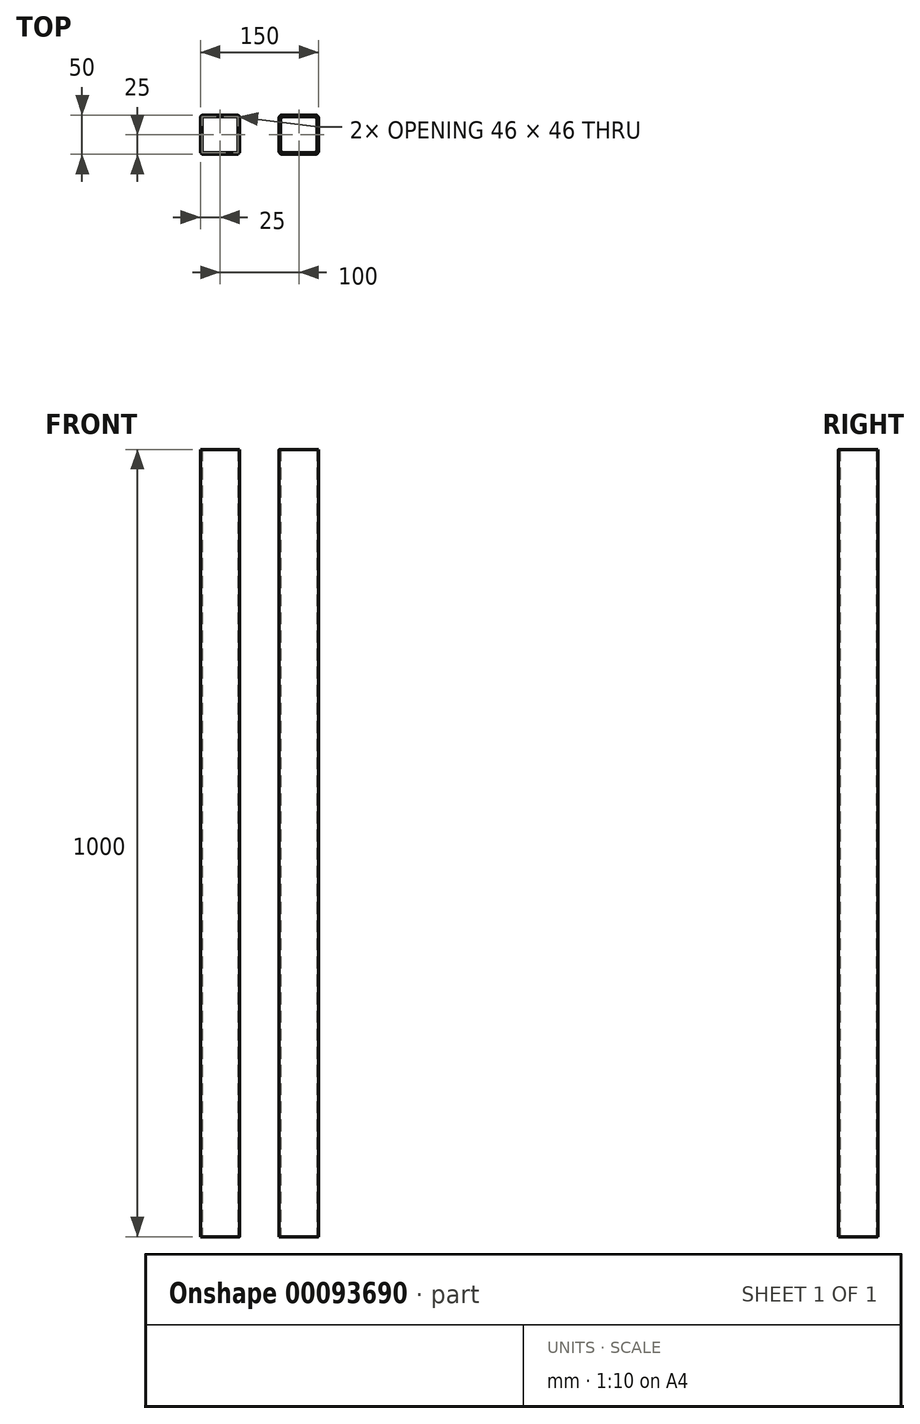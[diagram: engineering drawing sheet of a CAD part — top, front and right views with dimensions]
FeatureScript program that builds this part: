
annotation { "Feature Type Name" : "Feature", "Feature Type Description" : "" }
export const myFeature = defineFeature(function(context is Context, id is Id, definition is map)
    precondition{}
    {
        {
            var Q0;
            Q0=qCreatedBy(makeId("Top.planeOp"),FACE);
            var sketch = newSketch(context, id + "F0", { "sketchPlane" : qUnion([Q0])});
            skLineSegment(sketch, "E0.bottom", {"start": v(25, 25) * mm, "end": v(-25, 25) * mm});
            skLineSegment(sketch, "E0.top", {"start": v(25, -25) * mm, "end": v(-25, -25) * mm});
            skLineSegment(sketch, "E0.left", {"start": v(25, 25) * mm, "end": v(25, -25) * mm});
            skLineSegment(sketch, "E0.right", {"start": v(-25, 25) * mm, "end": v(-25, -25) * mm});
            skPoint(sketch, "E0.middle", {"position": v(0, 0) * mm});
            skLineSegment(sketch, "E1.bottom", {"start": v(23, 23) * mm, "end": v(-23, 23) * mm});
            skLineSegment(sketch, "E1.top", {"start": v(23, -23) * mm, "end": v(-23, -23) * mm});
            skLineSegment(sketch, "E1.left", {"start": v(23, 23) * mm, "end": v(23, -23) * mm});
            skLineSegment(sketch, "E1.right", {"start": v(-23, 23) * mm, "end": v(-23, -23) * mm});
            skSolve(sketch);
        }
        {
            var Q0;
            Q0 = qSketchRegion(id + "F0", true);
            extrude(context, id + "F1", {"entities" : qUnion([Q0]), "endBound" : BoundingType.SYMMETRIC, "depth" : 1000 * mm});
        }
        {
            var Q0;
            Q0=makeQuery(id+"F1.opExtrude","SWEPT_EDGE",EDGE,{"disambiguationData":[OSD([sQuery(id+"F0.wireOp",EDGE,"E0.bottom"),sQuery(id+"F0.wireOp",EDGE,"E0.left")])]});
            var Q1;
            Q1=makeQuery(id+"F1.opExtrude","SWEPT_EDGE",EDGE,{"disambiguationData":[OSD([sQuery(id+"F0.wireOp",EDGE,"E0.top"),sQuery(id+"F0.wireOp",EDGE,"E0.left")])]});
            var Q2;
            Q2=makeQuery(id+"F1.opExtrude","SWEPT_EDGE",EDGE,{"disambiguationData":[OSD([sQuery(id+"F0.wireOp",EDGE,"E0.bottom"),sQuery(id+"F0.wireOp",EDGE,"E0.right")])]});
            var Q3;
            Q3=makeQuery(id+"F1.opExtrude","SWEPT_EDGE",EDGE,{"disambiguationData":[OSD([sQuery(id+"F0.wireOp",EDGE,"E0.top"),sQuery(id+"F0.wireOp",EDGE,"E0.right")])]});
            var Q4;
            Q4=makeQuery(id+"F1.opExtrude","SWEPT_EDGE",EDGE,{"disambiguationData":[OSD([sQuery(id+"F0.wireOp",EDGE,"E1.top"),sQuery(id+"F0.wireOp",EDGE,"E1.right")])]});
            var Q5;
            Q5=makeQuery(id+"F1.opExtrude","SWEPT_EDGE",EDGE,{"disambiguationData":[OSD([sQuery(id+"F0.wireOp",EDGE,"E1.bottom"),sQuery(id+"F0.wireOp",EDGE,"E1.right")])]});
            var Q6;
            Q6=makeQuery(id+"F1.opExtrude","SWEPT_EDGE",EDGE,{"disambiguationData":[OSD([sQuery(id+"F0.wireOp",EDGE,"E1.bottom"),sQuery(id+"F0.wireOp",EDGE,"E1.left")])]});
            var Q7;
            Q7=makeQuery(id+"F1.opExtrude","SWEPT_EDGE",EDGE,{"disambiguationData":[OSD([sQuery(id+"F0.wireOp",EDGE,"E1.top"),sQuery(id+"F0.wireOp",EDGE,"E1.left")])]});
            fillet(context, id + "F2", {"entities" : qUnion([Q0, Q1, Q2, Q3, Q4, Q5, Q6, Q7]), "radius" : 4 * mm, "tangentPropagation" : true, "allowEdgeOverflow" : false});
        }
        {
            var Q0;
            Q0=makeQuery(id+"F1.opExtrude","SWEPT_BODY",BODY,{"disambiguationData":[OSD([sQuery(id+"F0.wireOp",EDGE,"E0.bottom"),sQuery(id+"F0.wireOp",EDGE,"E0.top"),sQuery(id+"F0.wireOp",EDGE,"E0.left"),sQuery(id+"F0.wireOp",EDGE,"E0.right"),sQuery(id+"F0.wireOp",EDGE,"E1.bottom"),sQuery(id+"F0.wireOp",EDGE,"E1.top"),sQuery(id+"F0.wireOp",EDGE,"E1.left"),sQuery(id+"F0.wireOp",EDGE,"E1.right")])]});
            var Q1;
            Q1=makeQuery(id+"F1.opExtrude","CAP_EDGE",EDGE,{"disambiguationData":[OSD([sQuery(id+"F0.wireOp",EDGE,"E1.bottom")])],"isStart":false});
            var Q2;
            Q2=makeQuery(id+"F1.opExtrude","CAP_EDGE",EDGE,{"disambiguationData":[OSD([sQuery(id+"F0.wireOp",EDGE,"E0.bottom")])],"isStart":false});
            transform(context, id + "F3", {"entities" : qUnion([Q0]), "transformType" : TransformType.TRANSLATION_DISTANCE, "transformDirection" : qUnion([Q2]), "distance" : 100 * mm, "makeCopy" : true});
        }
    });
